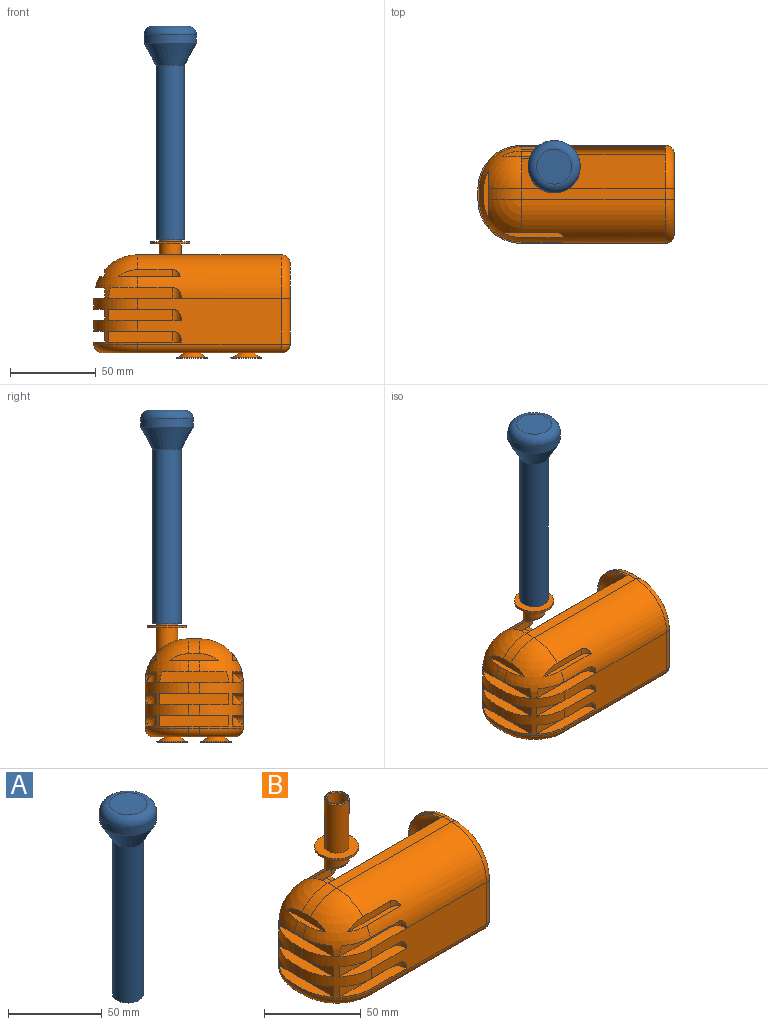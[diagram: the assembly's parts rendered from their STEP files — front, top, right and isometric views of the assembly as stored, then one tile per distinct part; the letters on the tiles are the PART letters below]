
ASSEMBLY  parts=2 mates=1
PART A: 9 faces, bbox 33x33x124.5 mm
  f0: cylinder r=6.35mm len=101.6mm, axis (0,0,-1), area 4053.7mm2, adj f2,f7
  f1: cylinder r=8.26mm len=101.6mm, axis (0,0,-1), area 5269.8mm2, adj f2,f3
  f2: plane 16.51x16.51mm, normal (0,0,-1), area 87.4mm2, adj f0,f1
  f3: cone r=8.26mm half-angle=28.8deg, axis (0,0,1), area 1069.8mm2, adj f1,f6
  f4: torus R=10.16mm, axis (0,0,1), area 671.5mm2, adj f5,f6
  f5: plane 20.32x20.32mm, normal (0,0,1), area 324.3mm2, adj f4
  f6: cylinder r=15.24mm len=30.48mm, axis (0,0,-1), area 486.4mm2, adj f3,f4
  f7: cone r=6.35mm half-angle=28.8deg, axis (0,0,1), area 896.4mm2, adj f0,f8
  f8: plane 26.67x26.67mm, normal (0,0,-1), area 558.6mm2, adj f7
PART B: 182 faces, bbox 116.4x61.3x98.4 mm
  f0: cylinder r=6.35mm len=29.97mm, axis (0,0,-1), area 1195.8mm2, adj f1,f103
  f1: plane 22.86x22.86mm, normal (0,0,1), area 283.8mm2, adj f0,f2
  f2: cylinder r=11.43mm len=22.86mm, axis (0,0,-1), area 91.2mm2, adj f1,f3
  f3: plane 22.86x22.86mm, normal (0,0,-1), area 283.8mm2, adj f2,f4
  f4: cylinder r=6.35mm len=14.95mm, axis (0,0,-1), area 414.6mm2, adj f3,f5
  f5: cylinder r=25.4mm len=83.82mm, axis (1,0,0), area -3216.6mm2, adj f4,f6,f94,f95,f96,f97,f98,f99
  f6: plane 83.82x6.35mm, normal (0,0,-1), area 532.3mm2, adj f5,f7,f92,f93
  f7: cylinder r=25.4mm len=83.82mm, axis (-1,0,0), area 3067mm2, adj f6,f8,f9,f10,f11,f87,f88,f89
  f8: plane 35.93x2.95mm, normal (0,0,-1), area 91.6mm2, adj f7,f9,f10,f11
  f9: cylinder r=5.08mm len=4.61mm, axis (0,0,-1), area 16.1mm2, adj f7,f8,f10
  f10: plane 31.32x4.1mm, normal (0,1,0), area 114.2mm2, adj f7,f8,f9,f11
  f11: sphere r=25.4mm, area 706.9mm2, adj f7,f8,f10,f12,f15,f82,f83,f84
  f12: plane 37.12x6.35mm, normal (0,1,0), area 233.1mm2, adj f11,f13,f14,f91
  f13: plane 42.2x6.35mm, normal (0,0,-1), area 228.9mm2, adj f12,f14,f15,f88,f89
  f14: cylinder r=5.08mm len=6.35mm, axis (0,0,-1), area 35.9mm2, adj f12,f13,f89,f90
  f15: cylinder r=25.4mm len=26.67mm, axis (0,0,1), area 597.8mm2, adj f11,f13,f16,f60,f61,f62,f63,f64
  f16: plane 6.35x6.35mm, normal (1,0,0), area 40.3mm2, adj f15,f17,f60,f81
  f17: cylinder r=25.4mm len=26.67mm, axis (0,0,-1), area 597.8mm2, adj f16,f18,f45,f49,f50,f51,f55,f56
  f18: torus R=20.32mm, axis (0,0,1), area 295.2mm2, adj f17,f19,f43,f44
  f19: plane 104.14x46.99mm, normal (0,0,1), area 4431.4mm2, adj f18,f20,f26,f27,f31,f35,f39,f43
  f20: cylinder r=5.08mm len=46.99mm, axis (0,1,0), area 375mm2, adj f19,f21,f24,f25
  f21: plane 46.99x46.99mm, normal (-1,0,0), area 2030.8mm2, adj f20,f22,f23,f87,f92,f94
  f22: cylinder r=5.08mm len=26.67mm, axis (0,0,-1), area 212.8mm2, adj f21,f25,f87,f88
  f23: cylinder r=5.08mm len=26.67mm, axis (0,0,1), area 212.8mm2, adj f21,f24,f94,f95
  f24: sphere r=5.08mm, area 40.5mm2, adj f20,f23,f43
  f25: sphere r=5.08mm, area 40.5mm2, adj f20,f22,f26
  f26: cylinder r=5.08mm len=83.82mm, axis (1,0,0), area 668.9mm2, adj f19,f25,f77,f88
  f27: torus R=10.62mm, axis (0,0,1), area 213.6mm2, adj f19,f28
  f28: torus R=8.91mm, axis (0,0,1), area 22.5mm2, adj f27,f29
  f29: torus R=10.62mm, axis (0,0,1), area 221.9mm2, adj f28,f30
  f30: plane 8.89x8.89mm, normal (0,0,1), area 62.1mm2, adj f29
  f31: torus R=10.62mm, axis (0,0,1), area 213.6mm2, adj f19,f32
  f32: torus R=8.91mm, axis (0,0,1), area 22.5mm2, adj f31,f33
  f33: torus R=10.62mm, axis (0,0,1), area 221.9mm2, adj f32,f34
  f34: plane 8.89x8.89mm, normal (0,0,1), area 62.1mm2, adj f33
  f35: torus R=10.62mm, axis (0,0,1), area 213.6mm2, adj f19,f36
  f36: torus R=8.91mm, axis (0,0,1), area 22.5mm2, adj f35,f37
  f37: torus R=10.62mm, axis (0,0,1), area 221.9mm2, adj f36,f38
  f38: plane 8.89x8.89mm, normal (0,0,1), area 62.1mm2, adj f37
  f39: torus R=10.62mm, axis (0,0,1), area 213.6mm2, adj f19,f40
  f40: torus R=8.91mm, axis (0,0,1), area 22.5mm2, adj f39,f41
  f41: torus R=10.62mm, axis (0,0,1), area 221.9mm2, adj f40,f42
  f42: plane 8.89x8.89mm, normal (0,0,1), area 62.1mm2, adj f41
  f43: cylinder r=5.08mm len=83.82mm, axis (-1,0,0), area 668.9mm2, adj f18,f19,f24,f95
  f44: cylinder r=5.08mm len=6.35mm, axis (0,-1,0), area 50.7mm2, adj f18,f19,f77,f78
  f45: plane 42.2x6.35mm, normal (0,0,-1), area 228.9mm2, adj f17,f46,f48,f49,f95
  f46: cylinder r=5.08mm len=6.35mm, axis (0,0,1), area 35.9mm2, adj f45,f47,f48,f49
  f47: cylinder r=5.08mm len=6.35mm, axis (0,1,0), area 35.9mm2, adj f46,f48,f50,f95
  f48: plane 1.27x1.27mm, normal (1,0,0), area 1.6mm2, adj f45,f46,f47,f95
  f49: plane 37.12x6.35mm, normal (0,-1,0), area 235.7mm2, adj f17,f45,f46,f50
  f50: plane 37.12x6.35mm, normal (0,0,1), area 202.1mm2, adj f17,f47,f49,f95
  f51: plane 42.2x6.35mm, normal (0,0,-1), area 228.9mm2, adj f17,f52,f54,f55,f95
  f52: cylinder r=5.08mm len=6.35mm, axis (0,0,1), area 35.9mm2, adj f51,f53,f54,f55
  f53: cylinder r=5.08mm len=6.35mm, axis (0,1,0), area 35.9mm2, adj f52,f54,f56,f95
  f54: plane 1.27x1.27mm, normal (1,0,0), area 1.6mm2, adj f51,f52,f53,f95
  f55: plane 37.12x6.35mm, normal (0,-1,0), area 235.7mm2, adj f17,f51,f52,f56
  f56: plane 37.12x6.35mm, normal (0,0,1), area 202.1mm2, adj f17,f53,f55,f95
  f57: plane 42.2x6.35mm, normal (0,0,-1), area 228.9mm2, adj f17,f58,f59,f95,f96
  f58: plane 37.12x6.35mm, normal (0,-1,0), area 233.1mm2, adj f57,f59,f98,f99
  f59: cylinder r=5.08mm len=6.35mm, axis (0,0,1), area 35.9mm2, adj f57,f58,f96,f97
  f60: plane 39.95x6.35mm, normal (0,0,-1), area 186.6mm2, adj f15,f16,f17,f61
  f61: plane 39.95x6.35mm, normal (1,0,0), area 253.7mm2, adj f15,f17,f60,f62
  f62: plane 39.95x6.35mm, normal (0,0,1), area 186.6mm2, adj f15,f17,f61,f63
  f63: plane 6.35x6.35mm, normal (1,0,0), area 40.3mm2, adj f15,f17,f62,f64
  f64: plane 39.95x6.35mm, normal (0,0,-1), area 186.6mm2, adj f15,f17,f63,f82
  f65: plane 37.12x6.35mm, normal (0,0,1), area 202.1mm2, adj f15,f66,f69,f88
  f66: cylinder r=5.08mm len=6.35mm, axis (0,1,0), area 35.9mm2, adj f65,f67,f68,f88
  f67: cylinder r=5.08mm len=6.35mm, axis (0,0,-1), area 35.9mm2, adj f66,f68,f69,f70
  f68: plane 1.27x1.27mm, normal (1,0,0), area 1.6mm2, adj f66,f67,f70,f88
  f69: plane 37.12x6.35mm, normal (0,1,0), area 235.7mm2, adj f15,f65,f67,f70
  f70: plane 42.2x6.35mm, normal (0,0,-1), area 228.9mm2, adj f15,f67,f68,f69,f88
  f71: plane 37.12x6.35mm, normal (0,0,1), area 202.1mm2, adj f15,f72,f75,f88
  f72: cylinder r=5.08mm len=6.35mm, axis (0,1,0), area 35.9mm2, adj f71,f73,f74,f88
  f73: cylinder r=5.08mm len=6.35mm, axis (0,0,-1), area 35.9mm2, adj f72,f74,f75,f76
  f74: plane 1.27x1.27mm, normal (1,0,0), area 1.6mm2, adj f72,f73,f76,f88
  f75: plane 37.12x6.35mm, normal (0,1,0), area 235.7mm2, adj f15,f71,f73,f76
  f76: plane 42.2x6.35mm, normal (0,0,-1), area 228.9mm2, adj f15,f73,f74,f75,f88
  f77: torus R=20.32mm, axis (0,0,1), area 295.2mm2, adj f15,f19,f26,f44
  f78: plane 6.35x1.27mm, normal (1,0,0), area 8.1mm2, adj f15,f17,f44,f79
  f79: plane 39.95x6.35mm, normal (0,0,-1), area 186.6mm2, adj f15,f17,f78,f80
  f80: plane 39.95x6.35mm, normal (1,0,0), area 253.7mm2, adj f15,f17,f79,f81
  f81: plane 39.95x6.35mm, normal (0,0,1), area 186.6mm2, adj f15,f16,f17,f80
  f82: plane 39.95x6.35mm, normal (1,0,0), area 248.5mm2, adj f11,f64,f83,f99
  f83: plane 37.46x5.54mm, normal (0,0,1), area 153mm2, adj f11,f82,f84,f99
  f84: cylinder r=25.4mm len=6.35mm, axis (0,1,0), area 43.7mm2, adj f11,f83,f85,f99
  f85: plane 28.35x2.95mm, normal (0,0,-1), area 62.5mm2, adj f11,f84,f86,f99
  f86: plane 28.35x4.1mm, normal (1,0,0), area 87.8mm2, adj f11,f85,f93,f99
  f87: torus R=20.32mm, axis (1,0,0), area 295.2mm2, adj f7,f21,f22,f92
  f88: plane 83.82x26.67mm, normal (0,1,0), area 1924mm2, adj f7,f13,f15,f22,f26,f65,f66,f68
  f89: plane 1.27x1.27mm, normal (1,0,0), area 1.6mm2, adj f7,f13,f14,f90
  f90: cylinder r=5.08mm len=6.32mm, axis (0,1,0), area 32.3mm2, adj f7,f14,f89,f91
  f91: plane 35.87x5.54mm, normal (0,0,1), area 171.6mm2, adj f7,f11,f12,f90
  f92: cylinder r=5.08mm len=6.35mm, axis (0,-1,0), area 50.7mm2, adj f6,f21,f87,f94
  f93: cylinder r=25.4mm len=19.05mm, axis (0,1,0), area 136.8mm2, adj f6,f11,f86,f99
  f94: torus R=20.32mm, axis (1,0,0), area 295.2mm2, adj f5,f21,f23,f92
  f95: plane 83.82x26.67mm, normal (0,-1,0), area 1924mm2, adj f5,f17,f23,f43,f45,f47,f48,f50
  f96: plane 1.27x1.27mm, normal (1,0,0), area 1.6mm2, adj f5,f57,f59,f97
  f97: cylinder r=5.08mm len=6.32mm, axis (0,1,0), area 32.3mm2, adj f5,f59,f96,f98
  f98: plane 35.87x5.54mm, normal (0,0,1), area 171.6mm2, adj f5,f58,f97,f99
  f99: sphere r=25.4mm, area 706.9mm2, adj f5,f17,f58,f82,f83,f84,f85,f86
  f100: plane 35.93x2.95mm, normal (0,0,-1), area 91.6mm2, adj f5,f99,f101,f102
  f101: cylinder r=5.08mm len=4.61mm, axis (0,0,1), area 16.1mm2, adj f5,f100,f102
  f102: plane 31.32x4.1mm, normal (0,-1,0), area 114.2mm2, adj f5,f99,f100,f101
  f103: torus R=5.84mm, axis (0,0,-1), area 30.9mm2, adj f0,f104
  f104: plane 11.68x11.68mm, normal (0,0,1), area 9.1mm2, adj f103,f105
  f105: torus R=5.59mm, axis (0,0,-1), area 26.4mm2, adj f104,f106
  f106: cylinder r=5.08mm len=46.68mm, axis (0,0,-1), area 1370.1mm2, adj f105,f107
  f107: cylinder r=24.13mm len=83.82mm, axis (1,0,0), area 2735.1mm2, adj f106,f108,f109,f110,f175,f176,f177,f178
  f108: cylinder r=6.35mm len=5.66mm, axis (0,0,1), area 23.5mm2, adj f107,f109,f181
  f109: plane 37.62x3.47mm, normal (0,0,-1), area 112mm2, adj f107,f108,f180,f181
  f110: plane 34.74x5.12mm, normal (0,0,1), area 154.3mm2, adj f107,f111,f175,f180
  f111: plane 36.63x8.89mm, normal (0,-1,0), area 321mm2, adj f110,f112,f174,f176,f180
  f112: cylinder r=24.13mm len=26.67mm, axis (0,0,-1), area 328.3mm2, adj f111,f113,f158,f159,f160,f161,f162,f165
  f113: plane 38.98x6.35mm, normal (0,0,1), area 182.5mm2, adj f112,f114,f158,f173
  f114: cylinder r=24.13mm len=26.67mm, axis (0,0,1), area 328.3mm2, adj f113,f115,f147,f148,f149,f152,f153,f154
  f115: sphere r=24.13mm, area 550.4mm2, adj f114,f116,f118,f119,f141,f142,f143,f144
  f116: plane 31.96x4.88mm, normal (0,1,0), area 138.4mm2, adj f115,f117,f118,f119
  f117: cylinder r=6.35mm len=5.66mm, axis (0,0,-1), area 23.5mm2, adj f116,f118,f119
  f118: plane 37.62x3.47mm, normal (0,0,-1), area 112mm2, adj f115,f116,f117,f119
  f119: cylinder r=24.13mm len=83.82mm, axis (-1,0,0), area 2832.2mm2, adj f115,f116,f117,f118,f120,f121,f122,f141
  f120: cylinder r=6.35mm len=8.89mm, axis (0,0,-1), area 65.6mm2, adj f119,f121,f147,f148,f154
  f121: cylinder r=6.35mm len=6.35mm, axis (0,1,0), area 33.6mm2, adj f119,f120,f141
  f122: torus R=20.32mm, axis (1,0,0), area 213.8mm2, adj f119,f123,f139,f140
  f123: cylinder r=3.81mm len=26.67mm, axis (0,0,-1), area 159.6mm2, adj f122,f124,f140,f154
  f124: sphere r=3.81mm, area 22.8mm2, adj f123,f125,f138
  f125: cylinder r=3.81mm len=83.82mm, axis (1,0,0), area 501.6mm2, adj f124,f126,f129,f154,f157
  f126: plane 42.98x6.35mm, normal (0,0,-1), area 231.8mm2, adj f125,f127,f156,f157
  f127: cylinder r=6.35mm len=8.89mm, axis (0,0,-1), area 65.7mm2, adj f126,f128,f154,f156
  f128: cylinder r=6.35mm len=6.35mm, axis (0,1,0), area 40.3mm2, adj f127,f154,f155
  f129: plane 104.14x46.99mm, normal (0,0,1), area 4716.3mm2, adj f125,f130,f136,f138,f157,f159
  f130: cylinder r=3.81mm len=83.82mm, axis (-1,0,0), area 501.6mm2, adj f129,f131,f133,f159,f177
  f131: sphere r=3.81mm, area 22.8mm2, adj f130,f132,f138
  f132: cylinder r=3.81mm len=26.67mm, axis (0,0,1), area 159.6mm2, adj f131,f140,f177,f178
  f133: plane 42.98x6.35mm, normal (0,0,-1), area 231.8mm2, adj f130,f134,f159,f160
  f134: cylinder r=6.35mm len=8.89mm, axis (0,0,1), area 65.7mm2, adj f133,f135,f160,f177
  f135: cylinder r=6.35mm len=6.35mm, axis (0,1,0), area 40.3mm2, adj f134,f161,f177
  f136: cylinder r=3.81mm len=6.35mm, axis (0,-1,0), area 38mm2, adj f129,f137,f157,f159
  f137: plane 38.98x6.35mm, normal (0,0,-1), area 182.5mm2, adj f136,f157,f158,f159
  f138: cylinder r=3.81mm len=46.99mm, axis (0,1,0), area 281.2mm2, adj f124,f129,f131,f140
  f139: cylinder r=3.81mm len=6.35mm, axis (0,-1,0), area 38mm2, adj f122,f140,f178,f179
  f140: plane 46.99x46.99mm, normal (-1,0,0), area 2030.8mm2, adj f122,f123,f132,f138,f139,f178
  f141: plane 34.74x5.12mm, normal (0,0,1), area 154.3mm2, adj f115,f119,f121,f147
  f142: plane 35.2x5.12mm, normal (0,0,1), area 133.3mm2, adj f115,f143,f167,f180
  f143: cylinder r=24.13mm len=6.35mm, axis (0,1,0), area 26.4mm2, adj f115,f142,f144,f180
  f144: plane 29.63x3.47mm, normal (0,0,-1), area 76.9mm2, adj f115,f143,f145,f180
  f145: plane 29.63x4.88mm, normal (1,0,0), area 109.4mm2, adj f115,f144,f146,f180
  f146: cylinder r=24.13mm len=17.78mm, axis (0,1,0), area 126.9mm2, adj f115,f145,f179,f180
  f147: plane 36.63x8.89mm, normal (0,1,0), area 321mm2, adj f114,f115,f120,f141,f148
  f148: plane 42.98x6.35mm, normal (0,0,-1), area 231.8mm2, adj f114,f120,f147,f154
  f149: plane 36.63x6.35mm, normal (0,0,1), area 200.1mm2, adj f114,f150,f152,f154
  f150: cylinder r=6.35mm len=6.35mm, axis (0,1,0), area 40.3mm2, adj f149,f151,f154
  f151: cylinder r=6.35mm len=8.89mm, axis (0,0,-1), area 65.7mm2, adj f150,f152,f153,f154
  f152: plane 36.63x8.89mm, normal (0,1,0), area 325.7mm2, adj f114,f149,f151,f153
  f153: plane 42.98x6.35mm, normal (0,0,-1), area 231.8mm2, adj f114,f151,f152,f154
  f154: plane 83.82x26.67mm, normal (0,1,0), area 1744.7mm2, adj f114,f119,f120,f123,f125,f127,f128,f148
  f155: plane 36.63x6.35mm, normal (0,0,1), area 200.1mm2, adj f114,f128,f154,f156
  f156: plane 36.63x8.89mm, normal (0,1,0), area 325.7mm2, adj f114,f126,f127,f155
  f157: torus R=20.32mm, axis (0,0,1), area 213.8mm2, adj f114,f125,f126,f129,f136,f137
  f158: plane 38.98x8.89mm, normal (1,0,0), area 346.5mm2, adj f112,f113,f114,f137
  f159: torus R=20.32mm, axis (0,0,1), area 213.8mm2, adj f112,f129,f130,f133,f136,f137
  f160: plane 36.63x8.89mm, normal (0,-1,0), area 325.7mm2, adj f112,f133,f134,f161
  f161: plane 36.63x6.35mm, normal (0,0,1), area 200.1mm2, adj f112,f135,f160,f177
  f162: plane 42.98x6.35mm, normal (0,0,-1), area 231.8mm2, adj f112,f163,f165,f177
  f163: cylinder r=6.35mm len=8.89mm, axis (0,0,1), area 65.7mm2, adj f162,f164,f165,f177
  f164: cylinder r=6.35mm len=6.35mm, axis (0,1,0), area 40.3mm2, adj f163,f166,f177
  f165: plane 36.63x8.89mm, normal (0,-1,0), area 325.7mm2, adj f112,f162,f163,f166
  f166: plane 36.63x6.35mm, normal (0,0,1), area 200.1mm2, adj f112,f164,f165,f177
  f167: plane 38.98x8.89mm, normal (1,0,0), area 337.1mm2, adj f112,f114,f115,f142,f168,f180
  f168: plane 38.98x6.35mm, normal (0,0,-1), area 182.5mm2, adj f112,f114,f167,f169
  f169: plane 6.35x3.81mm, normal (1,0,0), area 24.2mm2, adj f112,f114,f168,f170
  f170: plane 38.98x6.35mm, normal (0,0,1), area 182.5mm2, adj f112,f114,f169,f171
  f171: plane 38.98x8.89mm, normal (1,0,0), area 346.5mm2, adj f112,f114,f170,f172
  f172: plane 38.98x6.35mm, normal (0,0,-1), area 182.5mm2, adj f112,f114,f171,f173
  f173: plane 6.35x3.81mm, normal (1,0,0), area 24.2mm2, adj f112,f113,f114,f172
  f174: plane 42.98x6.35mm, normal (0,0,-1), area 231.8mm2, adj f111,f112,f176,f177
  f175: cylinder r=6.35mm len=6.35mm, axis (0,1,0), area 33.6mm2, adj f107,f110,f176
  f176: cylinder r=6.35mm len=8.89mm, axis (0,0,1), area 65.6mm2, adj f107,f111,f174,f175,f177
  f177: plane 83.82x26.67mm, normal (0,-1,0), area 1744.7mm2, adj f107,f112,f130,f132,f134,f135,f161,f162
  f178: torus R=20.32mm, axis (1,0,0), area 213.8mm2, adj f107,f132,f139,f140
  f179: plane 83.82x6.35mm, normal (0,0,-1), area 532.3mm2, adj f107,f119,f139,f146
  f180: sphere r=24.13mm, area 550.4mm2, adj f107,f109,f110,f111,f112,f142,f143,f144
  f181: plane 31.96x4.88mm, normal (0,-1,0), area 138.4mm2, adj f107,f108,f109,f180
PLACE A t=(-10.16,-3.17,-30.48)mm
PLACE B rot(axis=(0,0,-1),0deg) t=(-10.16,-3.17,-31.75)mm fixed
MATE slider A.f0 <-> B.f0  axis (0,0,-1) through (-22.86,12.7,34.29)mm
